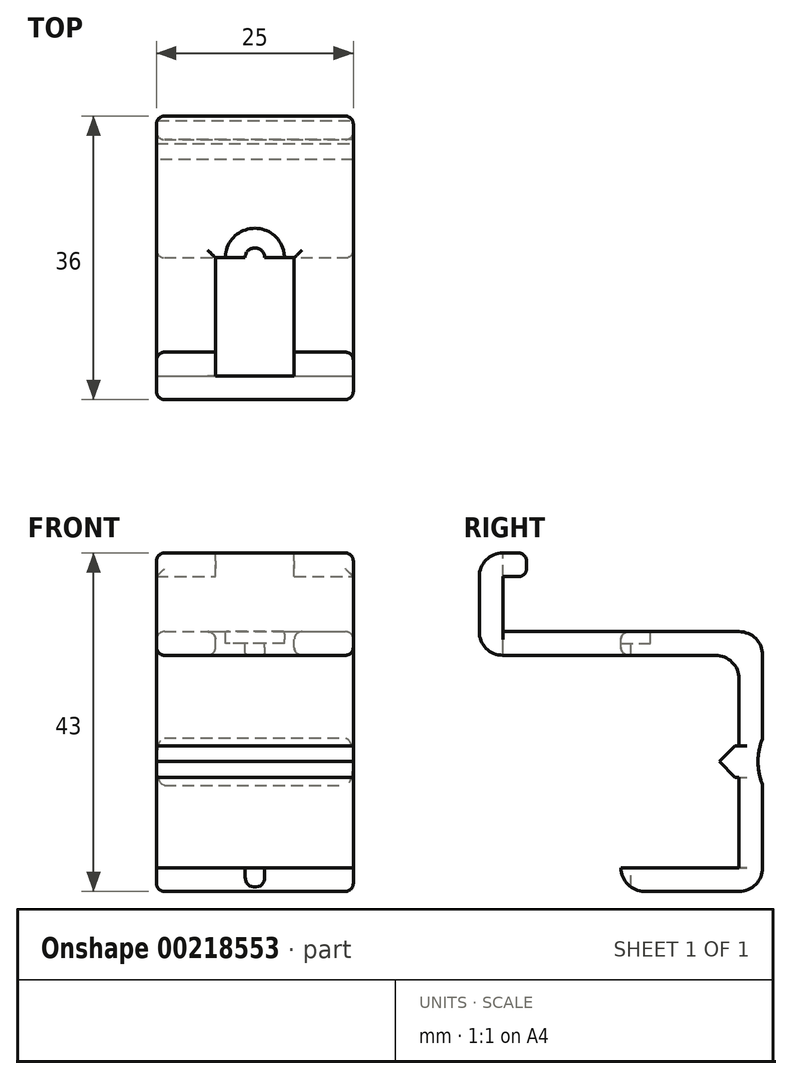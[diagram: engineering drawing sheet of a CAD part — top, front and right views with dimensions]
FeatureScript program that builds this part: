
annotation { "Feature Type Name" : "Feature", "Feature Type Description" : "" }
export const myFeature = defineFeature(function(context is Context, id is Id, definition is map)
    precondition{}
    {
        {
            var Q0;
            Q0=qCreatedBy(makeId("Top.planeOp"),FACE);
            var sketch = newSketch(context, id + "F0", { "sketchPlane" : qUnion([Q0])});
            skLineSegment(sketch, "E0.bottom", {"start": v(-12.5, 18) * mm, "end": v(12.5, 18) * mm});
            skLineSegment(sketch, "E0.top", {"start": v(-12.5, -18) * mm, "end": v(12.5, -18) * mm});
            skLineSegment(sketch, "E0.left", {"start": v(-12.5, 18) * mm, "end": v(-12.5, -18) * mm});
            skLineSegment(sketch, "E0.right", {"start": v(12.5, 18) * mm, "end": v(12.5, -18) * mm});
            skPoint(sketch, "E1", {"position": v(12.5, 0) * mm});
            skPoint(sketch, "E2", {"position": v(0, 18) * mm});
            skSolve(sketch);
        }
        {
            var Q0;
            Q0=makeQuery(id+"F0.imprint","IMPRINT",FACE,{"disambiguationData":[TD([[makeQuery(id+"F0.imprint","IMPRINT",EDGE,{"derivedFrom":sQuery(id+"F0.wireOp",EDGE,"E0.bottom")}),-1.0]])]});
            extrude(context, id + "F1", {"entities" : qUnion([Q0]), "depth" : 3 * mm});
        }
        {
            var Q0;
            Q0=makeQuery(id+"F1.opExtrude","CAP_FACE",FACE,{"disambiguationData":[OSD([sQuery(id+"F0.wireOp",EDGE,"E0.bottom"),sQuery(id+"F0.wireOp",EDGE,"E0.top"),sQuery(id+"F0.wireOp",EDGE,"E0.left"),sQuery(id+"F0.wireOp",EDGE,"E0.right")])],"isStart":false});
            var sketch = newSketch(context, id + "F2", { "sketchPlane" : qUnion([Q0])});
            skLineSegment(sketch, "E3.bottom", {"start": v(-12.5, 18) * mm, "end": v(12.5, 18) * mm});
            skLineSegment(sketch, "E3.top", {"start": v(-12.5, 15) * mm, "end": v(12.5, 15) * mm});
            skLineSegment(sketch, "E3.left", {"start": v(-12.5, 18) * mm, "end": v(-12.5, 15) * mm});
            skLineSegment(sketch, "E3.right", {"start": v(12.5, 18) * mm, "end": v(12.5, 15) * mm});
            skLineSegment(sketch, "E4.bottom", {"start": v(-12.5, -18) * mm, "end": v(12.5, -18) * mm});
            skLineSegment(sketch, "E4.top", {"start": v(-12.5, -15) * mm, "end": v(12.5, -15) * mm});
            skLineSegment(sketch, "E4.left", {"start": v(-12.5, -18) * mm, "end": v(-12.5, -15) * mm});
            skLineSegment(sketch, "E4.right", {"start": v(12.5, -18) * mm, "end": v(12.5, -15) * mm});
            skPoint(sketch, "E5", {"position": v(0, 0) * mm});
            skLineSegment(sketch, "E6.bottom", {"start": v(-5, -18) * mm, "end": v(5, -18) * mm});
            skLineSegment(sketch, "E6.top", {"start": v(-5, 0) * mm, "end": v(5, 0) * mm});
            skLineSegment(sketch, "E6.left", {"start": v(-5, -18) * mm, "end": v(-5, 0) * mm});
            skLineSegment(sketch, "E6.right", {"start": v(5, -18) * mm, "end": v(5, 0) * mm});
            skSolve(sketch);
        }
        {
            var Q0;
            Q0=makeQuery(id+"F2.imprint","IMPRINT",FACE,{"disambiguationData":[TD([[makeQuery(id+"F2.imprint","IMPRINT",EDGE,{"derivedFrom":sQuery(id+"F2.wireOp",EDGE,"E4.bottom")}),1.0]])]});
            extrude(context, id + "F3", {"entities" : qUnion([Q0]), "operationType" : NewBodyOperationType.ADD, "depth" : 10 * mm});
        }
        {
            var Q0;
            Q0=makeQuery(id+"F2.imprint","IMPRINT",FACE,{"disambiguationData":[TD([[makeQuery(id+"F2.imprint","IMPRINT",EDGE,{"derivedFrom":sQuery(id+"F2.wireOp",EDGE,"E3.bottom")}),-1.0]])]});
            extrude(context, id + "F4", {"entities" : qUnion([Q0]), "operationType" : NewBodyOperationType.ADD, "oppositeDirection" : true, "depth" : 33 * mm});
        }
        {
            var Q0;
            Q0=makeQuery(id+"F3.opExtrude","SWEPT_FACE",FACE,{"disambiguationData":[OSD([sQuery(id+"F2.wireOp",EDGE,"E4.top")])]});
            var sketch = newSketch(context, id + "F5", { "sketchPlane" : qUnion([Q0])});
            skLineSegment(sketch, "E7.bottom", {"start": v(12.5, 13) * mm, "end": v(-12.5, 13) * mm});
            skLineSegment(sketch, "E7.top", {"start": v(12.5, 10) * mm, "end": v(-12.5, 10) * mm});
            skLineSegment(sketch, "E7.left", {"start": v(12.5, 13) * mm, "end": v(12.5, 10) * mm});
            skLineSegment(sketch, "E7.right", {"start": v(-12.5, 13) * mm, "end": v(-12.5, 10) * mm});
            skSolve(sketch);
        }
        {
            var Q0;
            Q0=makeQuery(id+"F5.imprint","IMPRINT",FACE,{"disambiguationData":[TD([[makeQuery(id+"F5.imprint","IMPRINT",EDGE,{"derivedFrom":sQuery(id+"F5.wireOp",EDGE,"E7.bottom")}),1.0]])]});
            extrude(context, id + "F6", {"entities" : qUnion([Q0]), "operationType" : NewBodyOperationType.ADD, "depth" : 3 * mm});
        }
        {
            var Q0;
            Q0=makeQuery(id+"F4.opExtrude","SWEPT_FACE",FACE,{"disambiguationData":[OSD([sQuery(id+"F2.wireOp",EDGE,"E3.top")])]});
            var sketch = newSketch(context, id + "F7", { "sketchPlane" : qUnion([Q0])});
            skLineSegment(sketch, "E8.bottom", {"start": v(-12.5, -30) * mm, "end": v(12.5, -30) * mm});
            skLineSegment(sketch, "E8.top", {"start": v(-12.5, -27) * mm, "end": v(12.5, -27) * mm});
            skLineSegment(sketch, "E8.left", {"start": v(-12.5, -30) * mm, "end": v(-12.5, -27) * mm});
            skLineSegment(sketch, "E8.right", {"start": v(12.5, -30) * mm, "end": v(12.5, -27) * mm});
            skSolve(sketch);
        }
        {
            var Q0;
            Q0=makeQuery(id+"F7.imprint","IMPRINT",FACE,{"disambiguationData":[TD([[makeQuery(id+"F7.imprint","IMPRINT",EDGE,{"derivedFrom":sQuery(id+"F7.wireOp",EDGE,"E8.bottom")}),1.0]])]});
            extrude(context, id + "F8", {"entities" : qUnion([Q0]), "operationType" : NewBodyOperationType.ADD, "depth" : 15 * mm});
        }
        {
            var Q0;
            Q0=makeQuery(id+"F8.boolean.opBoolean","MERGE",FACE,{"derivedFrom":[makeQuery(id+"F6.boolean.opBoolean","MERGE",FACE,{"derivedFrom":[makeQuery(id+"F4.boolean.opBoolean","MERGE",FACE,{"derivedFrom":[makeQuery(id+"F3.boolean.opBoolean","MERGE",FACE,{"derivedFrom":[makeQuery(id+"F1.opExtrude","SWEPT_FACE",FACE,{"disambiguationData":[OSD([sQuery(id+"F0.wireOp",EDGE,"E0.right")])]}),makeQuery(id+"F3.opExtrude","SWEPT_FACE",FACE,{"disambiguationData":[OSD([sQuery(id+"F2.wireOp",EDGE,"E4.right")])]})]}),makeQuery(id+"F4.opExtrude","SWEPT_FACE",FACE,{"disambiguationData":[OSD([sQuery(id+"F2.wireOp",EDGE,"E3.right")])]})]}),makeQuery(id+"F6.opExtrude","SWEPT_FACE",FACE,{"disambiguationData":[OSD([sQuery(id+"F5.wireOp",EDGE,"E7.right")])]})]}),makeQuery(id+"F8.opExtrude","SWEPT_FACE",FACE,{"disambiguationData":[OSD([sQuery(id+"F7.wireOp",EDGE,"E8.right")])]})]});
            var sketch = newSketch(context, id + "F9", { "sketchPlane" : qUnion([Q0])});
            skArc(sketch, "E9", {"start": v(18, -10.5) * mm, "mid": v(17.42, -13.5) * mm, "end": v(18, -16.5) * mm});
            skSolve(sketch);
        }
        {
            var Q0;
            {var subQ0=sQuery(id+"F9.wireOp",EDGE,"E9");Q0=makeQuery(id+"F9.imprint","IMPRINT",FACE,{"disambiguationData":[TD([[makeQuery(id+"F9.imprint","IMPRINT",EDGE,{"derivedFrom":subQ0}),1.0]])]});}
            extrude(context, id + "F10", {"entities" : qUnion([Q0]), "operationType" : NewBodyOperationType.REMOVE, "endBound" : BoundingType.UP_TO_NEXT, "oppositeDirection" : true, "depth" : 25 * mm});
        }
        {
            var Q0;
            Q0=makeQuery(id+"F4.opExtrude","SWEPT_FACE",FACE,{"disambiguationData":[OSD([sQuery(id+"F2.wireOp",EDGE,"E3.top")])]});
            var sketch = newSketch(context, id + "F11", { "sketchPlane" : qUnion([Q0])});
            skLineSegment(sketch, "E10", {"start": v(-12.5, -13.5) * mm, "end": v(-12.5, -11.5) * mm});
            skLineSegment(sketch, "E11", {"start": v(-12.5, -11.5) * mm, "end": v(12.5, -11.5) * mm});
            skLineSegment(sketch, "E12", {"start": v(12.5, -11.5) * mm, "end": v(12.5, -13.5) * mm});
            skLineSegment(sketch, "E13", {"start": v(12.5, -13.5) * mm, "end": v(12.5, -15.5) * mm});
            skLineSegment(sketch, "E14", {"start": v(12.5, -15.5) * mm, "end": v(-12.5, -15.5) * mm});
            skLineSegment(sketch, "E15", {"start": v(-12.5, -15.5) * mm, "end": v(-12.5, -13.5) * mm});
            skSolve(sketch);
        }
        {
            var Q0;
            Q0=makeQuery(id+"F11.imprint","IMPRINT",FACE,{"disambiguationData":[TD([[makeQuery(id+"F11.imprint","IMPRINT",EDGE,{"derivedFrom":sQuery(id+"F11.wireOp",EDGE,"E10")}),-1.0]])]});
            extrude(context, id + "F12", {"entities" : qUnion([Q0]), "operationType" : NewBodyOperationType.ADD, "depth" : 2.5 * mm});
        }
        {
            var Q0;
            Q0=makeQuery(id+"F12.opExtrude","CAP_EDGE",EDGE,{"disambiguationData":[OSD([sQuery(id+"F11.wireOp",EDGE,"E11")])],"isStart":false});
            var Q1;
            Q1=makeQuery(id+"F12.opExtrude","CAP_EDGE",EDGE,{"disambiguationData":[OSD([sQuery(id+"F11.wireOp",EDGE,"E14")])],"isStart":false});
            chamfer(context, id + "F13", {"entities" : qUnion([Q0, Q1]), "width" : 2 * mm, "tangentPropagation" : true});
        }
        {
            var Q0;
            Q0=makeQuery(id+"F8.opExtrude","CAP_EDGE",EDGE,{"disambiguationData":[OSD([sQuery(id+"F7.wireOp",EDGE,"E8.top")])],"isStart":true});
            var Q1;
            Q1=makeQuery(id+"F4.boolean.opBoolean","INTERSECT",EDGE,{"derivedFrom":[makeQuery(id+"F1.opExtrude","CAP_FACE",FACE,{"disambiguationData":[OSD([sQuery(id+"F0.wireOp",EDGE,"E0.bottom"),sQuery(id+"F0.wireOp",EDGE,"E0.top"),sQuery(id+"F0.wireOp",EDGE,"E0.left"),sQuery(id+"F0.wireOp",EDGE,"E0.right")])],"isStart":true}),makeQuery(id+"F4.opExtrude","SWEPT_FACE",FACE,{"disambiguationData":[OSD([sQuery(id+"F2.wireOp",EDGE,"E3.top")])]})]});
            var Q2;
            Q2=makeQuery(id+"F1.opExtrude","CAP_EDGE",EDGE,{"disambiguationData":[OSD([sQuery(id+"F0.wireOp",EDGE,"E0.bottom")])],"isStart":false});
            var Q3;
            Q3=makeQuery(id+"F4.opExtrude","CAP_EDGE",EDGE,{"disambiguationData":[OSD([sQuery(id+"F2.wireOp",EDGE,"E3.bottom")])],"isStart":false});
            var Q4;
            Q4=makeQuery(id+"F8.opExtrude","CAP_EDGE",EDGE,{"disambiguationData":[OSD([sQuery(id+"F7.wireOp",EDGE,"E8.bottom")])],"isStart":false});
            var Q5;
            Q5=makeQuery(id+"F1.opExtrude","CAP_EDGE",EDGE,{"disambiguationData":[OSD([sQuery(id+"F0.wireOp",EDGE,"E0.top")])],"isStart":true});
            var Q6;
            Q6=makeQuery(id+"F3.opExtrude","CAP_EDGE",EDGE,{"disambiguationData":[OSD([sQuery(id+"F2.wireOp",EDGE,"E4.bottom")])],"isStart":false});
            fillet(context, id + "F14", {"entities" : qUnion([Q0, Q1, Q2, Q3, Q4, Q5, Q6]), "radius" : 3 * mm, "tangentPropagation" : true, "allowEdgeOverflow" : false});
        }
        {
            var Q0;
            {var subQ5=sQuery(id+"F2.wireOp",EDGE,"E6.top");Q0=makeQuery(id+"F2.imprint","IMPRINT",FACE,{"disambiguationData":[TD([[makeQuery(id+"F2.imprint","IMPRINT",EDGE,{"derivedFrom":subQ5}),-1.0]])]});}
            var Q1;
            {var subQ5=sQuery(id+"F2.wireOp",EDGE,"E6.bottom");Q1=makeQuery(id+"F2.imprint","IMPRINT",FACE,{"disambiguationData":[TD([[makeQuery(id+"F2.imprint","IMPRINT",EDGE,{"derivedFrom":subQ5}),1.0]])]});}
            extrude(context, id + "F15", {"entities" : qUnion([Q0, Q1]), "operationType" : NewBodyOperationType.REMOVE, "endBound" : BoundingType.SYMMETRIC, "oppositeDirection" : true, "depth" : 25 * mm});
        }
        {
            var Q0;
            Q0=makeQuery(id+"F3.opExtrude","CAP_EDGE",EDGE,{"disambiguationData":[OSD([sQuery(id+"F2.wireOp",EDGE,"E4.top")])],"isStart":true});
            var Q1;
            Q1=makeQuery(id+"F6.opExtrude","CAP_EDGE",EDGE,{"disambiguationData":[OSD([sQuery(id+"F5.wireOp",EDGE,"E7.top")])],"isStart":true});
            var Q2;
            Q2=makeQuery(id+"F6.opExtrude","CAP_EDGE",EDGE,{"disambiguationData":[OSD([sQuery(id+"F5.wireOp",EDGE,"E7.bottom")])],"isStart":false});
            var Q3;
            Q3=makeQuery(id+"F6.opExtrude","CAP_EDGE",EDGE,{"disambiguationData":[OSD([sQuery(id+"F5.wireOp",EDGE,"E7.top")])],"isStart":false});
            var Q4;
            Q4=makeQuery(id+"F4.boolean.opBoolean","MERGE",EDGE,{"derivedFrom":[makeQuery(id+"F1.opExtrude","SWEPT_EDGE",EDGE,{"disambiguationData":[OSD([sQuery(id+"F0.wireOp",EDGE,"E0.bottom"),sQuery(id+"F0.wireOp",EDGE,"E0.left")])]}),makeQuery(id+"F4.opExtrude","SWEPT_EDGE",EDGE,{"disambiguationData":[OSD([sQuery(id+"F2.wireOp",EDGE,"E3.bottom"),sQuery(id+"F2.wireOp",EDGE,"E3.left")])]})]});
            var Q5;
            Q5=makeQuery(id+"F1.opExtrude","CAP_EDGE",EDGE,{"disambiguationData":[OSD([sQuery(id+"F0.wireOp",EDGE,"E0.left")])],"isStart":false});
            var Q6;
            Q6=makeQuery(id+"F4.boolean.opBoolean","MERGE",EDGE,{"derivedFrom":[makeQuery(id+"F1.opExtrude","SWEPT_EDGE",EDGE,{"disambiguationData":[OSD([sQuery(id+"F0.wireOp",EDGE,"E0.bottom"),sQuery(id+"F0.wireOp",EDGE,"E0.right")])]}),makeQuery(id+"F4.opExtrude","SWEPT_EDGE",EDGE,{"disambiguationData":[OSD([sQuery(id+"F2.wireOp",EDGE,"E3.bottom"),sQuery(id+"F2.wireOp",EDGE,"E3.right")])]})]});
            var Q7;
            Q7=makeQuery(id+"F4.opExtrude","SWEPT_EDGE",EDGE,{"disambiguationData":[OSD([sQuery(id+"F0.wireOp",EDGE,"E0.left"),sQuery(id+"F2.wireOp",EDGE,"E3.top"),sQuery(id+"F2.wireOp",EDGE,"E3.left")])]});
            var Q8;
            Q8=makeQuery(id+"F1.opExtrude","CAP_EDGE",EDGE,{"disambiguationData":[OSD([sQuery(id+"F0.wireOp",EDGE,"E0.left")])],"isStart":true});
            var Q9;
            Q9=makeQuery(id+"F1.opExtrude","CAP_EDGE",EDGE,{"disambiguationData":[OSD([sQuery(id+"F0.wireOp",EDGE,"E0.right")])],"isStart":false});
            var Q10;
            Q10=makeQuery(id+"F1.opExtrude","CAP_EDGE",EDGE,{"disambiguationData":[OSD([sQuery(id+"F0.wireOp",EDGE,"E0.right")])],"isStart":true});
            var Q11;
            Q11=makeQuery(id+"F3.boolean.opBoolean","MERGE",EDGE,{"derivedFrom":[makeQuery(id+"F1.opExtrude","SWEPT_EDGE",EDGE,{"disambiguationData":[OSD([sQuery(id+"F0.wireOp",EDGE,"E0.top"),sQuery(id+"F0.wireOp",EDGE,"E0.right")])]}),makeQuery(id+"F3.opExtrude","SWEPT_EDGE",EDGE,{"disambiguationData":[OSD([sQuery(id+"F2.wireOp",EDGE,"E4.bottom"),sQuery(id+"F2.wireOp",EDGE,"E4.right")])]})]});
            var Q12;
            Q12=makeQuery(id+"F6.opExtrude","CAP_EDGE",EDGE,{"disambiguationData":[OSD([sQuery(id+"F5.wireOp",EDGE,"E7.left")])],"isStart":false});
            var Q13;
            Q13=makeQuery(id+"F6.opExtrude","CAP_EDGE",EDGE,{"disambiguationData":[OSD([sQuery(id+"F5.wireOp",EDGE,"E7.right")])],"isStart":false});
            var Q14;
            Q14=makeQuery(id+"F15.boolean.opBoolean","INTERSECT",EDGE,{"derivedFrom":[makeQuery(id+"F1.opExtrude","CAP_FACE",FACE,{"disambiguationData":[OSD([sQuery(id+"F0.wireOp",EDGE,"E0.bottom"),sQuery(id+"F0.wireOp",EDGE,"E0.top"),sQuery(id+"F0.wireOp",EDGE,"E0.left"),sQuery(id+"F0.wireOp",EDGE,"E0.right")])],"isStart":false}),makeQuery(id+"F15.opExtrude","SWEPT_FACE",FACE,{"disambiguationData":[OSD([sQuery(id+"F2.wireOp",EDGE,"E6.left")])]})]});
            var Q15;
            Q15=makeQuery(id+"F15.boolean.opBoolean","INTERSECT",EDGE,{"derivedFrom":[makeQuery(id+"F1.opExtrude","CAP_FACE",FACE,{"disambiguationData":[OSD([sQuery(id+"F0.wireOp",EDGE,"E0.bottom"),sQuery(id+"F0.wireOp",EDGE,"E0.top"),sQuery(id+"F0.wireOp",EDGE,"E0.left"),sQuery(id+"F0.wireOp",EDGE,"E0.right")])],"isStart":true}),makeQuery(id+"F15.opExtrude","SWEPT_FACE",FACE,{"disambiguationData":[OSD([sQuery(id+"F2.wireOp",EDGE,"E6.left")])]})]});
            var Q16;
            Q16=makeQuery(id+"F15.boolean.opBoolean","INTERSECT",EDGE,{"derivedFrom":[makeQuery(id+"F1.opExtrude","CAP_FACE",FACE,{"disambiguationData":[OSD([sQuery(id+"F0.wireOp",EDGE,"E0.bottom"),sQuery(id+"F0.wireOp",EDGE,"E0.top"),sQuery(id+"F0.wireOp",EDGE,"E0.left"),sQuery(id+"F0.wireOp",EDGE,"E0.right")])],"isStart":false}),makeQuery(id+"F15.opExtrude","SWEPT_FACE",FACE,{"disambiguationData":[OSD([sQuery(id+"F2.wireOp",EDGE,"E6.right")])]})]});
            var Q17;
            Q17=makeQuery(id+"F15.boolean.opBoolean","INTERSECT",EDGE,{"derivedFrom":[makeQuery(id+"F1.opExtrude","CAP_FACE",FACE,{"disambiguationData":[OSD([sQuery(id+"F0.wireOp",EDGE,"E0.bottom"),sQuery(id+"F0.wireOp",EDGE,"E0.top"),sQuery(id+"F0.wireOp",EDGE,"E0.left"),sQuery(id+"F0.wireOp",EDGE,"E0.right")])],"isStart":false}),makeQuery(id+"F15.opExtrude","SWEPT_FACE",FACE,{"disambiguationData":[OSD([sQuery(id+"F2.wireOp",EDGE,"E6.top")])]})]});
            var Q18;
            Q18=makeQuery(id+"F15.boolean.opBoolean","INTERSECT",EDGE,{"derivedFrom":[makeQuery(id+"F1.opExtrude","CAP_FACE",FACE,{"disambiguationData":[OSD([sQuery(id+"F0.wireOp",EDGE,"E0.bottom"),sQuery(id+"F0.wireOp",EDGE,"E0.top"),sQuery(id+"F0.wireOp",EDGE,"E0.left"),sQuery(id+"F0.wireOp",EDGE,"E0.right")])],"isStart":true}),makeQuery(id+"F15.opExtrude","SWEPT_FACE",FACE,{"disambiguationData":[OSD([sQuery(id+"F2.wireOp",EDGE,"E6.right")])]})]});
            var Q19;
            Q19=makeQuery(id+"F15.boolean.opBoolean","INTERSECT",EDGE,{"derivedFrom":[makeQuery(id+"F1.opExtrude","CAP_FACE",FACE,{"disambiguationData":[OSD([sQuery(id+"F0.wireOp",EDGE,"E0.bottom"),sQuery(id+"F0.wireOp",EDGE,"E0.top"),sQuery(id+"F0.wireOp",EDGE,"E0.left"),sQuery(id+"F0.wireOp",EDGE,"E0.right")])],"isStart":true}),makeQuery(id+"F15.opExtrude","SWEPT_FACE",FACE,{"disambiguationData":[OSD([sQuery(id+"F2.wireOp",EDGE,"E6.top")])]})]});
            fillet(context, id + "F16", {"entities" : qUnion([Q0, Q1, Q2, Q3, Q4, Q5, Q6, Q7, Q8, Q9, Q10, Q11, Q12, Q13, Q14, Q15, Q16, Q17, Q18, Q19]), "radius" : 1 * mm, "tangentPropagation" : true, "allowEdgeOverflow" : false});
        }
        {
            var Q0;
            Q0=sQuery(id+"F2.wireOp",VERTEX,"E5");
            var Q1;
            Q1=makeQuery(id+"F1.opExtrude","SWEPT_BODY",BODY,{"disambiguationData":[OSD([sQuery(id+"F0.wireOp",EDGE,"E0.bottom"),sQuery(id+"F0.wireOp",EDGE,"E0.top"),sQuery(id+"F0.wireOp",EDGE,"E0.left"),sQuery(id+"F0.wireOp",EDGE,"E0.right")])]});
            hole(context, id + "F17", {"style" : HoleStyle.C_BORE, "endStyle" : HoleEndStyle.THROUGH, "holeDiameter" : 2.5 * mm, "cBoreDiameter" : 7.5 * mm, "cBoreDepth" : 1.5 * mm, "startFromSketch" : true, "locations" : qUnion([Q0]), "scope" : qUnion([Q1]), "isTappedThrough" : true});
        }
    });
